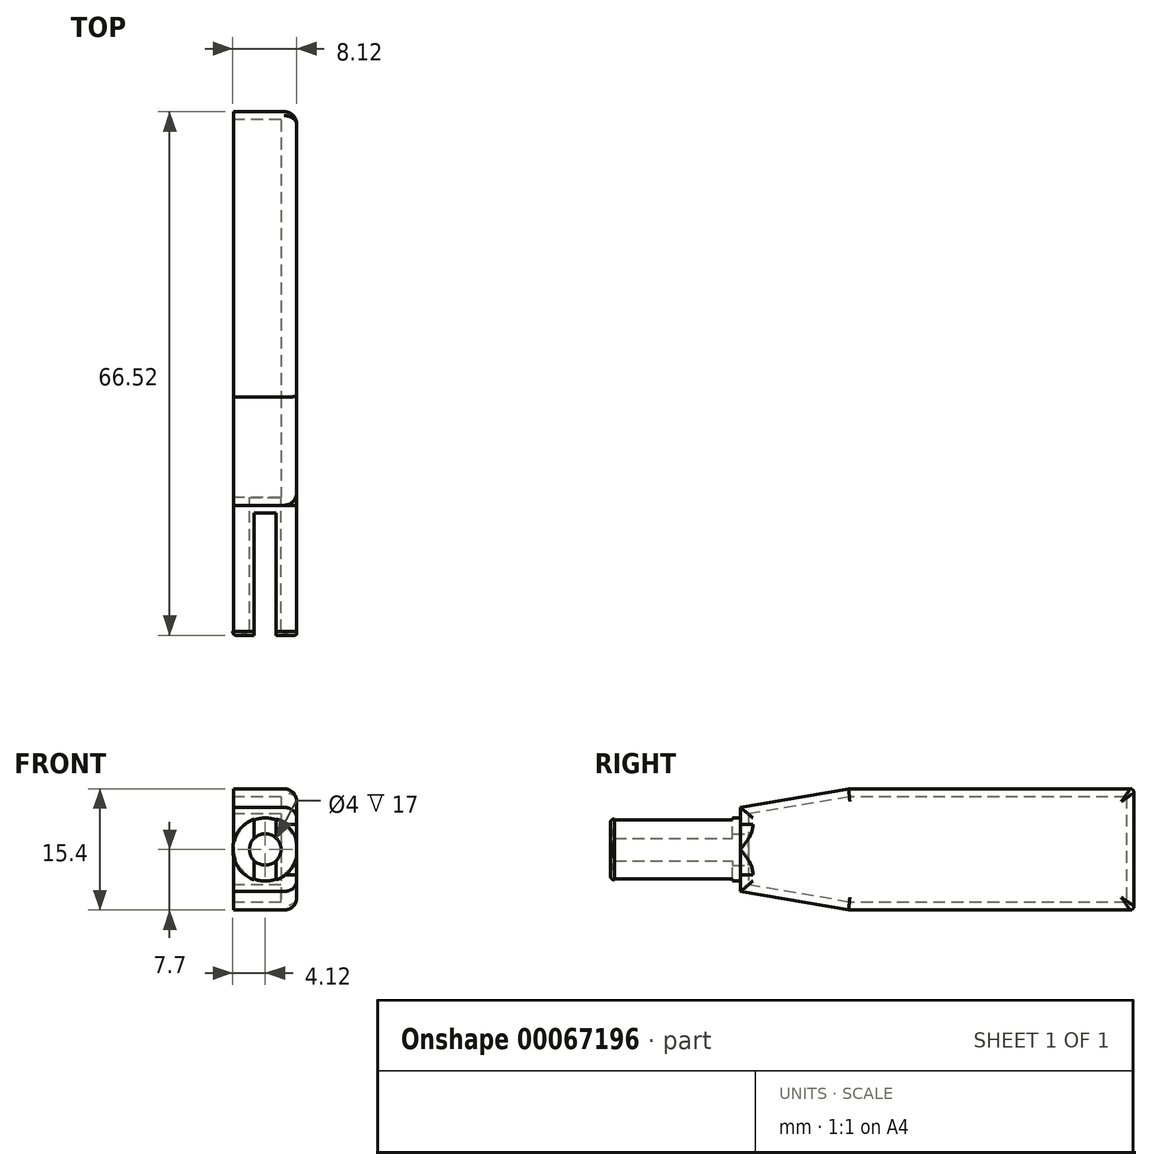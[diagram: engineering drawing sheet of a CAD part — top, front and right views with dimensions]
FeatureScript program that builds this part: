
annotation { "Feature Type Name" : "Feature", "Feature Type Description" : "" }
export const myFeature = defineFeature(function(context is Context, id is Id, definition is map)
    precondition{}
    {
        {
            var Q0;
            Q0=qCreatedBy(makeId("Right.planeOp"),FACE);
            var sketch = newSketch(context, id + "F0", { "sketchPlane" : qUnion([Q0])});
            skLineSegment(sketch, "E0", {"start": v(48, 6.7) * mm, "end": v(48, -6.7) * mm});
            skLineSegment(sketch, "E1", {"start": v(0, 4.5) * mm, "end": v(0, -4.5) * mm});
            skLineSegment(sketch, "E2", {"start": v(48, 6.7) * mm, "end": v(12.84, 6.7) * mm});
            skLineSegment(sketch, "E3", {"start": v(48, -6.7) * mm, "end": v(12.84, -6.7) * mm});
            skLineSegment(sketch, "E4", {"start": v(12.84, 6.7) * mm, "end": v(0, 4.5) * mm});
            skLineSegment(sketch, "E5", {"start": v(12.84, -6.7) * mm, "end": v(0, -4.5) * mm});
            skLineSegment(sketch, "E6.0", {"start": v(49, 7.7) * mm, "end": v(12.75, 7.7) * mm});
            skLineSegment(sketch, "E6.1", {"start": v(49, -7.7) * mm, "end": v(12.75, -7.7) * mm});
            skLineSegment(sketch, "E6.2", {"start": v(12.75, -7.7) * mm, "end": v(-1, -5.34) * mm});
            skLineSegment(sketch, "E6.3", {"start": v(49, 7.7) * mm, "end": v(49, -7.7) * mm});
            skLineSegment(sketch, "E6.4", {"start": v(-1, 5.34) * mm, "end": v(-1, -5.34) * mm});
            skLineSegment(sketch, "E6.5", {"start": v(12.75, 7.7) * mm, "end": v(-1, 5.34) * mm});
            skSolve(sketch);
        }
        {
            var Q0;
            Q0 = qSketchRegion(id + "F0", true);
            extrude(context, id + "F1", {"entities" : qUnion([Q0]), "depth" : 8 * mm, "symmetric" : true});
        }
        {
            var Q0;
            Q0=makeQuery(id+"F1.opExtrude","SWEPT_FACE",FACE,{"disambiguationData":[OSD([sQuery(id+"F0.wireOp",EDGE,"E6.4")])]});
            var sketch = newSketch(context, id + "F2", { "sketchPlane" : qUnion([Q0])});
            skCircle(sketch, "E7", {"center": v(0, 0) * mm, "radius": 4 * mm});
            skCircle(sketch, "E8", {"center": v(0, 0) * mm, "radius": 2 * mm});
            skSolve(sketch);
        }
        {
            var Q0;
            Q0=makeQuery(id+"F2.imprint","IMPRINT",FACE,{"disambiguationData":[TD([[makeQuery(id+"F2.imprint","IMPRINT",EDGE,{"derivedFrom":sQuery(id+"F2.wireOp",EDGE,"E8")}),-1.0]])]});
            extrude(context, id + "F3", {"entities" : qUnion([Q0]), "operationType" : NewBodyOperationType.ADD, "depth" : 16 * mm});
        }
        {
            var Q0;
            Q0=makeQuery(id+"F3.boolean.opBoolean","SPLIT",FACE,{"disambiguationData":[TD([makeQuery(id+"F3.opExtrude","SWEPT_FACE",FACE,{"disambiguationData":[OSD([sQuery(id+"F2.wireOp",EDGE,"E8")])]})])],"derivedFrom":makeQuery(id+"F1.opExtrude","SWEPT_FACE",FACE,{"disambiguationData":[OSD([sQuery(id+"F0.wireOp",EDGE,"E6.4")])]})});
            extrude(context, id + "F4", {"entities" : qUnion([Q0]), "operationType" : NewBodyOperationType.REMOVE, "oppositeDirection" : true, "depth" : 2 * mm});
        }
        {
            var Q0;
            Q0=makeQuery(id+"F1.opExtrude","CAP_FACE",FACE,{"disambiguationData":[OSD([sQuery(id+"F0.wireOp",EDGE,"E0"),sQuery(id+"F0.wireOp",EDGE,"E1"),sQuery(id+"F0.wireOp",EDGE,"E2"),sQuery(id+"F0.wireOp",EDGE,"E3"),sQuery(id+"F0.wireOp",EDGE,"E4"),sQuery(id+"F0.wireOp",EDGE,"E5"),sQuery(id+"F0.wireOp",EDGE,"E6.0"),sQuery(id+"F0.wireOp",EDGE,"E6.1"),sQuery(id+"F0.wireOp",EDGE,"E6.2"),sQuery(id+"F0.wireOp",EDGE,"E6.3"),sQuery(id+"F0.wireOp",EDGE,"E6.4"),sQuery(id+"F0.wireOp",EDGE,"E6.5")])],"isStart":false});
            var sketch = newSketch(context, id + "F5", { "sketchPlane" : qUnion([Q0])});
            skPoint(sketch, "E9.0", {"position": v(-1, 5.34) * mm});
            skPoint(sketch, "E10.0", {"position": v(12.75, 7.7) * mm});
            skPoint(sketch, "E11.0", {"position": v(49, 7.7) * mm});
            skPoint(sketch, "E12.0", {"position": v(49, -7.7) * mm});
            skPoint(sketch, "E13.0", {"position": v(12.75, -7.7) * mm});
            skPoint(sketch, "E14.0", {"position": v(-1, -5.34) * mm});
            skLineSegment(sketch, "E15", {"start": v(-1, 5.34) * mm, "end": v(-1, -5.34) * mm});
            skLineSegment(sketch, "E16", {"start": v(-1, -5.34) * mm, "end": v(12.75, -7.7) * mm});
            skLineSegment(sketch, "E17", {"start": v(12.75, -7.7) * mm, "end": v(49, -7.7) * mm});
            skLineSegment(sketch, "E18", {"start": v(49, -7.7) * mm, "end": v(49, 7.7) * mm});
            skLineSegment(sketch, "E19", {"start": v(49, 7.7) * mm, "end": v(12.75, 7.7) * mm});
            skLineSegment(sketch, "E20", {"start": v(12.75, 7.7) * mm, "end": v(-1, 5.34) * mm});
            skSolve(sketch);
        }
        {
            var Q0;
            Q0 = qSketchRegion(id + "F5", true);
            extrude(context, id + "F6", {"entities" : qUnion([Q0]), "operationType" : NewBodyOperationType.ADD, "oppositeDirection" : true, "depth" : 2 * mm});
        }
        {
            var Q0;
            Q0=makeQuery(id+"F1.opExtrude","CAP_EDGE",EDGE,{"disambiguationData":[OSD([sQuery(id+"F0.wireOp",EDGE,"E6.1")])],"isStart":false});
            var Q1;
            Q1=makeQuery(id+"F1.opExtrude","CAP_EDGE",EDGE,{"disambiguationData":[OSD([sQuery(id+"F0.wireOp",EDGE,"E6.3")])],"isStart":false});
            var Q2;
            Q2=makeQuery(id+"F1.opExtrude","CAP_EDGE",EDGE,{"disambiguationData":[OSD([sQuery(id+"F0.wireOp",EDGE,"E6.0")])],"isStart":false});
            var Q3;
            Q3=makeQuery(id+"F1.opExtrude","CAP_EDGE",EDGE,{"disambiguationData":[OSD([sQuery(id+"F0.wireOp",EDGE,"E6.5")])],"isStart":false});
            var Q4;
            Q4=makeQuery(id+"F1.opExtrude","CAP_EDGE",EDGE,{"disambiguationData":[OSD([sQuery(id+"F0.wireOp",EDGE,"E6.2")])],"isStart":false});
            var Q5;
            {var subQ0=sQuery(id+"F0.wireOp",EDGE,"E6.5");var subQ1=sQuery(id+"F0.wireOp",EDGE,"E6.4");Q5=makeQuery(id+"F3.boolean.opBoolean","SPLIT",EDGE,{"disambiguationData":[TD([makeQuery(id+"F1.opExtrude","SWEPT_FACE",FACE,{"disambiguationData":[OSD([subQ0])]})])],"derivedFrom":makeQuery(id+"F1.opExtrude","CAP_EDGE",EDGE,{"disambiguationData":[OSD([subQ1])],"isStart":false})});}
            var Q6;
            {var subQ0=sQuery(id+"F0.wireOp",EDGE,"E6.4");var subQ1=sQuery(id+"F0.wireOp",EDGE,"E6.2");Q6=makeQuery(id+"F3.boolean.opBoolean","SPLIT",EDGE,{"disambiguationData":[TD([makeQuery(id+"F1.opExtrude","SWEPT_FACE",FACE,{"disambiguationData":[OSD([subQ1])]})])],"derivedFrom":makeQuery(id+"F1.opExtrude","CAP_EDGE",EDGE,{"disambiguationData":[OSD([subQ0])],"isStart":false})});}
            fillet(context, id + "F7", {"entities" : qUnion([Q0, Q1, Q2, Q3, Q4, Q5, Q6]), "radius" : 1.6 * mm, "tangentPropagation" : true, "allowEdgeOverflow" : false});
        }
        {
            var Q0;
            Q0=qCreatedBy(makeId("Right.planeOp"),FACE);
            var sketch = newSketch(context, id + "F8", { "sketchPlane" : qUnion([Q0])});
            skFitSpline(sketch, "E21", {"points": [v(-17, 3.97) * mm, v(-17.4, 3.95) * mm, v(-17.51, 3.6) * mm, v(-17.48, 3.28) * mm, v(-17.37, 2.83) * mm, v(-17.18, 2.3) * mm, v(-17, 2) * mm], "startDerivative": vector(-0.03, 5.09) * mm, "endDerivative": vector(2.6, -4.38) * mm});
            skPoint(sketch, "E22.0", {"position": v(0, 0) * mm});
            skLineSegment(sketch, "E23", {"start": v(-17, 3.97) * mm, "end": v(-17, 2) * mm});
            skSolve(sketch);
        }
        {
            var Q0;
            Q0 = qSketchRegion(id + "F8", true);
            var Q1;
            Q1=makeQuery(id+"F3.opExtrude","CAP_EDGE",EDGE,{"disambiguationData":[OSD([sQuery(id+"F2.wireOp",EDGE,"E8")])],"isStart":false});
            revolve(context, id + "F9", {"operationType" : NewBodyOperationType.ADD, "entities" : qUnion([Q0]), "axis" : qUnion([Q1]), "revolveType" : RevolveType.FULL});
        }
        {
            var Q0;
            Q0=qCreatedBy(makeId("Right.planeOp"),FACE);
            var sketch = newSketch(context, id + "F10", { "sketchPlane" : qUnion([Q0])});
            skLineSegment(sketch, "E24.bottom", {"start": v(-2.32, 0) * mm, "end": v(-14.34, 0) * mm});
            skLineSegment(sketch, "E24.top", {"start": v(-2.32, -1.3) * mm, "end": v(-14.34, -1.3) * mm});
            skLineSegment(sketch, "E24.left", {"start": v(-2.32, 0) * mm, "end": v(-2.32, -1.3) * mm});
            skLineSegment(sketch, "E24.right", {"start": v(-14.34, 0) * mm, "end": v(-14.34, -1.3) * mm});
            skSolve(sketch);
        }
        {
            var Q0;
            Q0=qCreatedBy(makeId("Top.planeOp"),FACE);
            var sketch = newSketch(context, id + "F11", { "sketchPlane" : qUnion([Q0])});
            skLineSegment(sketch, "E25", {"start": v(-1.4, -2) * mm, "end": v(1.4, -2) * mm});
            skLineSegment(sketch, "E26", {"start": v(1.4, -2) * mm, "end": v(1.4, -18) * mm});
            skLineSegment(sketch, "E27", {"start": v(1.4, -18) * mm, "end": v(-1.4, -18) * mm});
            skLineSegment(sketch, "E28", {"start": v(-1.4, -18) * mm, "end": v(-1.4, -2) * mm});
            skSolve(sketch);
        }
        {
            var Q0;
            Q0 = qSketchRegion(id + "F11", true);
            extrude(context, id + "F12", {"entities" : qUnion([Q0]), "operationType" : NewBodyOperationType.REMOVE, "oppositeDirection" : true, "depth" : 25 * mm, "symmetric" : true});
        }
        {
            var Q0;
            Q0=makeQuery(id+"F1.opExtrude","SWEPT_EDGE",EDGE,{"disambiguationData":[OSD([sQuery(id+"F0.wireOp",EDGE,"E6.1"),sQuery(id+"F0.wireOp",EDGE,"E6.3")])]});
            var Q1;
            Q1=makeQuery(id+"F7.opFillet","BLEND_EDGE",EDGE,{"blendedFrom":[makeQuery(id+"F1.opExtrude","CAP_EDGE",EDGE,{"disambiguationData":[OSD([sQuery(id+"F0.wireOp",EDGE,"E6.1")])],"isStart":false}),makeQuery(id+"F1.opExtrude","CAP_EDGE",EDGE,{"disambiguationData":[OSD([sQuery(id+"F0.wireOp",EDGE,"E6.3")])],"isStart":false})],"blendedInto":[]});
            var Q2;
            Q2=makeQuery(id+"F1.opExtrude","SWEPT_EDGE",EDGE,{"disambiguationData":[OSD([sQuery(id+"F0.wireOp",EDGE,"E6.0"),sQuery(id+"F0.wireOp",EDGE,"E6.3")])]});
            var Q3;
            Q3=makeQuery(id+"F7.opFillet","BLEND_EDGE",EDGE,{"blendedFrom":[makeQuery(id+"F1.opExtrude","CAP_EDGE",EDGE,{"disambiguationData":[OSD([sQuery(id+"F0.wireOp",EDGE,"E6.0")])],"isStart":false}),makeQuery(id+"F1.opExtrude","CAP_EDGE",EDGE,{"disambiguationData":[OSD([sQuery(id+"F0.wireOp",EDGE,"E6.3")])],"isStart":false})],"blendedInto":[]});
            fillet(context, id + "F13", {"entities" : qUnion([Q0, Q1, Q2, Q3]), "radius" : .5 * mm, "tangentPropagation" : true, "allowEdgeOverflow" : false});
        }
        {
            var Q0;
            Q0=makeQuery(id+"F6.boolean.opBoolean","MERGE",FACE,{"derivedFrom":[makeQuery(id+"F1.opExtrude","CAP_FACE",FACE,{"disambiguationData":[OSD([sQuery(id+"F0.wireOp",EDGE,"E0"),sQuery(id+"F0.wireOp",EDGE,"E1"),sQuery(id+"F0.wireOp",EDGE,"E2"),sQuery(id+"F0.wireOp",EDGE,"E3"),sQuery(id+"F0.wireOp",EDGE,"E4"),sQuery(id+"F0.wireOp",EDGE,"E5"),sQuery(id+"F0.wireOp",EDGE,"E6.0"),sQuery(id+"F0.wireOp",EDGE,"E6.1"),sQuery(id+"F0.wireOp",EDGE,"E6.2"),sQuery(id+"F0.wireOp",EDGE,"E6.3"),sQuery(id+"F0.wireOp",EDGE,"E6.4"),sQuery(id+"F0.wireOp",EDGE,"E6.5")])],"isStart":false}),makeQuery(id+"F6.opExtrude","CAP_FACE",FACE,{"disambiguationData":[OSD([sQuery(id+"F5.wireOp",EDGE,"E15"),sQuery(id+"F5.wireOp",EDGE,"E16"),sQuery(id+"F5.wireOp",EDGE,"E17"),sQuery(id+"F5.wireOp",EDGE,"E18"),sQuery(id+"F5.wireOp",EDGE,"E19"),sQuery(id+"F5.wireOp",EDGE,"E20")])],"isStart":true})]});
            var sketch = newSketch(context, id + "F14", { "sketchPlane" : qUnion([Q0])});
            skLineSegment(sketch, "E29.bottom", {"start": v(-13.12, -7.23) * mm, "end": v(-21.95, -7.23) * mm});
            skLineSegment(sketch, "E29.top", {"start": v(-13.12, 7.43) * mm, "end": v(-21.95, 7.43) * mm});
            skLineSegment(sketch, "E29.left", {"start": v(-13.12, -7.23) * mm, "end": v(-13.12, 7.43) * mm});
            skLineSegment(sketch, "E29.right", {"start": v(-21.95, -7.23) * mm, "end": v(-21.95, 7.43) * mm});
            skSolve(sketch);
        }
        {
            var Q0;
            Q0 = qSketchRegion(id + "F14", true);
            extrude(context, id + "F15", {"entities" : qUnion([Q0]), "operationType" : NewBodyOperationType.REMOVE, "depth" : 1 * mm});
        }
    });
